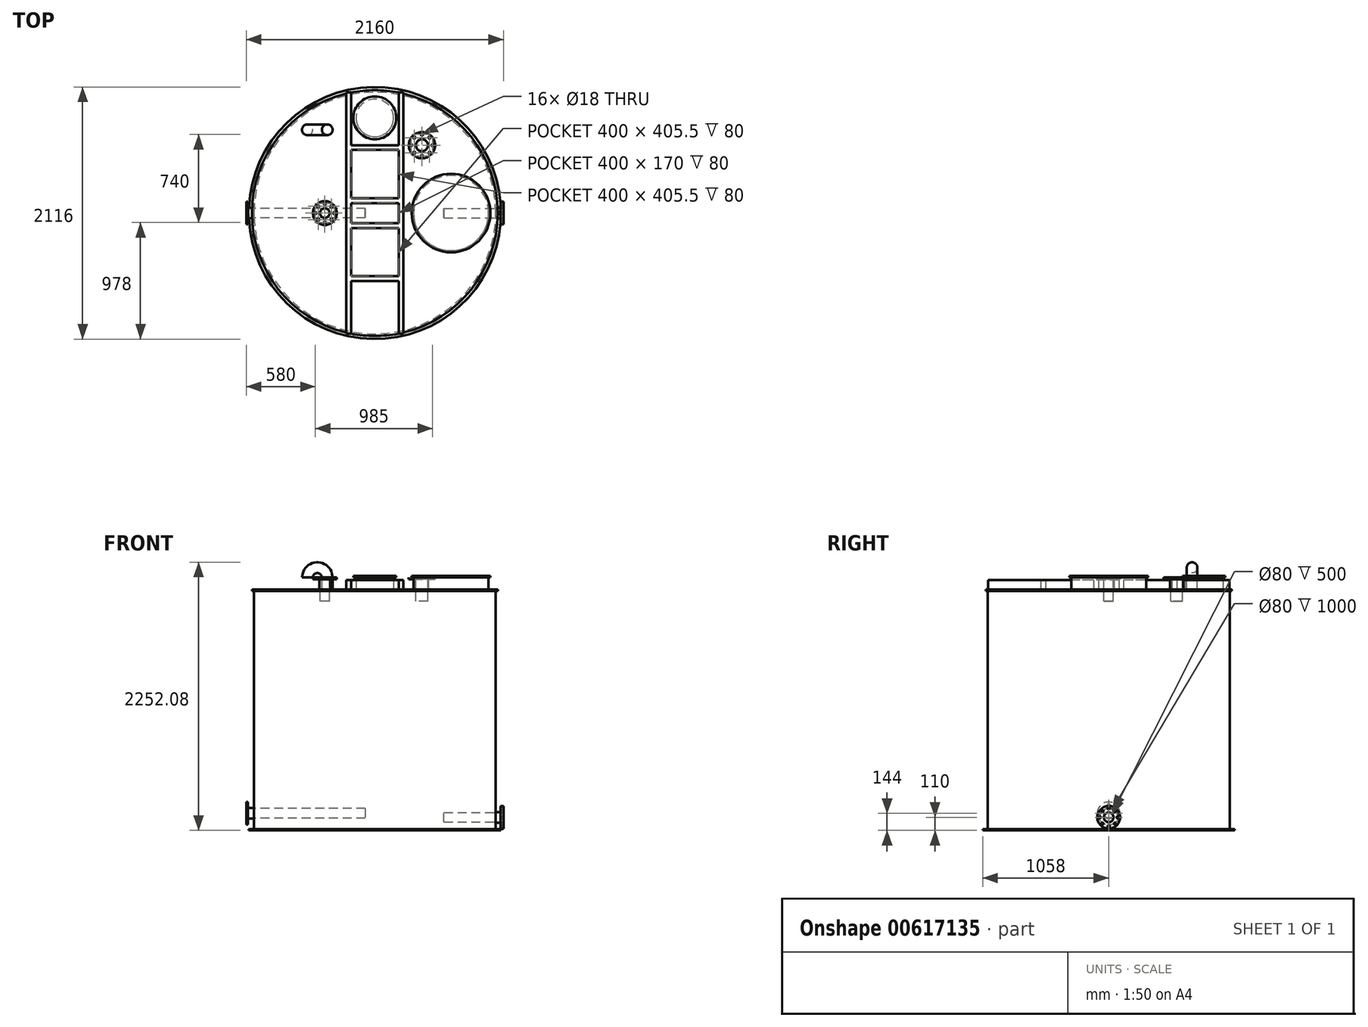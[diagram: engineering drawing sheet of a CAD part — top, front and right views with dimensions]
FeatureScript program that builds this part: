
annotation { "Feature Type Name" : "Feature", "Feature Type Description" : "" }
export const myFeature = defineFeature(function(context is Context, id is Id, definition is map)
    precondition{}
    {
        {
            var Q0;
            Q0=qCreatedBy(makeId("Front.planeOp"),FACE);
            var sketch = newSketch(context, id + "F0", { "sketchPlane" : qUnion([Q0])});
            skLineSegment(sketch, "E0.bottom", {"start": v(0, 0) * mm, "end": v(1015, 0) * mm});
            skLineSegment(sketch, "E0.top", {"start": v(0, 2024) * mm, "end": v(1015, 2024) * mm});
            skLineSegment(sketch, "E0.left", {"start": v(0, 0) * mm, "end": v(0, 2024) * mm});
            skLineSegment(sketch, "E0.right", {"start": v(1015, 12) * mm, "end": v(1015, 2012) * mm});
            skLineSegment(sketch, "E1.bottom", {"start": v(1015, 0) * mm, "end": v(1058, 0) * mm});
            skLineSegment(sketch, "E1.top", {"start": v(1015, 12) * mm, "end": v(1058, 12) * mm});
            skLineSegment(sketch, "E1.right", {"start": v(1058, 0) * mm, "end": v(1058, 12) * mm});
            skLineSegment(sketch, "E2.bottom", {"start": v(1015, 2024) * mm, "end": v(1032, 2024) * mm});
            skLineSegment(sketch, "E2.top", {"start": v(1015, 2012) * mm, "end": v(1032, 2012) * mm});
            skLineSegment(sketch, "E2.right", {"start": v(1032, 2024) * mm, "end": v(1032, 2012) * mm});
            skSolve(sketch);
        }
        {
            var Q0;
            Q0=makeQuery(id+"F0.imprint","IMPRINT",FACE,{"disambiguationData":[TD([[makeQuery(id+"F0.imprint","IMPRINT",EDGE,{"derivedFrom":sQuery(id+"F0.wireOp",EDGE,"E0.bottom")}),1.0]])]});
            var Q1;
            Q1=sQuery(id+"F0.wireOp",EDGE,"E0.left");
            revolve(context, id + "F1", {"entities" : qUnion([Q0]), "axis" : qUnion([Q1]), "revolveType" : RevolveType.FULL});
        }
        {
            var Q0;
            Q0=makeQuery(id+"F1.opRevolve","SWEPT_FACE",FACE,{"disambiguationData":[OSD([sQuery(id+"F0.wireOp",EDGE,"E0.top"),sQuery(id+"F0.wireOp",EDGE,"E2.bottom")])]});
            var sketch = newSketch(context, id + "F2", { "sketchPlane" : qUnion([Q0])});
            skLineSegment(sketch, "E3.bottom", {"start": v(-240, 1012.5) * mm, "end": v(-200, 1012.5) * mm});
            skLineSegment(sketch, "E3.top", {"start": v(-240, -1012.5) * mm, "end": v(-200, -1012.5) * mm});
            skLineSegment(sketch, "E3.left", {"start": v(-240, 1012.5) * mm, "end": v(-240, -1012.5) * mm});
            skLineSegment(sketch, "E3.right", {"start": v(-200, 1012.5) * mm, "end": v(-200, 570.5) * mm});
            skLineSegment(sketch, "E4.bottom", {"start": v(200, 1012.5) * mm, "end": v(240, 1012.5) * mm});
            skLineSegment(sketch, "E4.top", {"start": v(200, -1012.5) * mm, "end": v(240, -1012.5) * mm});
            skLineSegment(sketch, "E4.left", {"start": v(200, 1012.5) * mm, "end": v(200, 570.5) * mm});
            skLineSegment(sketch, "E4.right", {"start": v(240, 1012.5) * mm, "end": v(240, -1012.5) * mm});
            skLineSegment(sketch, "E5.bottom", {"start": v(-200, 85) * mm, "end": v(200, 85) * mm});
            skLineSegment(sketch, "E5.top", {"start": v(-200, 125) * mm, "end": v(200, 125) * mm});
            skLineSegment(sketch, "E6.bottom", {"start": v(-200, -85) * mm, "end": v(200, -85) * mm});
            skLineSegment(sketch, "E6.top", {"start": v(-200, -125) * mm, "end": v(200, -125) * mm});
            skLineSegment(sketch, "E7.bottom", {"start": v(-200, 570.5) * mm, "end": v(200, 570.5) * mm});
            skLineSegment(sketch, "E7.top", {"start": v(-200, 530.5) * mm, "end": v(200, 530.5) * mm});
            skLineSegment(sketch, "E8.bottom", {"start": v(-200, -530.5) * mm, "end": v(200, -530.5) * mm});
            skLineSegment(sketch, "E8.top", {"start": v(-200, -570.5) * mm, "end": v(200, -570.5) * mm});
            skLineSegment(sketch, "E9.trimOffspring", {"start": v(-200, 530.5) * mm, "end": v(-200, 125) * mm});
            skLineSegment(sketch, "E10.trimOffspring", {"start": v(200, 530.5) * mm, "end": v(200, 125) * mm});
            skLineSegment(sketch, "E11.trimOffspring", {"start": v(-200, 85) * mm, "end": v(-200, -85) * mm});
            skLineSegment(sketch, "E12.trimOffspring", {"start": v(200, 85) * mm, "end": v(200, -85) * mm});
            skLineSegment(sketch, "E13.trimOffspring", {"start": v(-200, -125) * mm, "end": v(-200, -530.5) * mm});
            skLineSegment(sketch, "E14.trimOffspring", {"start": v(200, -125) * mm, "end": v(200, -530.5) * mm});
            skLineSegment(sketch, "E15.trimOffspring", {"start": v(-200, -570.5) * mm, "end": v(-200, -1012.5) * mm});
            skLineSegment(sketch, "E16.trimOffspring", {"start": v(200, -570.5) * mm, "end": v(200, -1012.5) * mm});
            skSolve(sketch);
        }
        {
            var Q0;
            Q0 = qSketchRegion(id + "F2", true);
            extrude(context, id + "F3", {"entities" : qUnion([Q0]), "operationType" : NewBodyOperationType.ADD, "depth" : 80 * mm, "offsetDistance" : 25 * mm});
        }
        {
            var Q0;
            {var subQ0=sQuery(id+"F2.wireOp",EDGE,"E4.right");Q0=makeQuery(id+"F3.boolean.opBoolean","SPLIT",FACE,{"disambiguationData":[TD([makeQuery(id+"F3.opExtrude","SWEPT_FACE",FACE,{"disambiguationData":[OSD([subQ0])]})])],"derivedFrom":makeQuery(id+"F1.opRevolve","SWEPT_FACE",FACE,{"disambiguationData":[OSD([sQuery(id+"F0.wireOp",EDGE,"E0.top"),sQuery(id+"F0.wireOp",EDGE,"E2.bottom")])]})});}
            var sketch = newSketch(context, id + "F4", { "sketchPlane" : qUnion([Q0])});
            skCircle(sketch, "E17", {"center": v(640, 0) * mm, "radius": 315 * mm});
            skSolve(sketch);
        }
        {
            var Q0;
            Q0=makeQuery(id+"F4.imprint","IMPRINT",FACE,{"disambiguationData":[TD([[makeQuery(id+"F4.imprint","IMPRINT",EDGE,{"derivedFrom":sQuery(id+"F4.wireOp",EDGE,"E17")}),1.0]])]});
            extrude(context, id + "F5", {"entities" : qUnion([Q0]), "operationType" : NewBodyOperationType.ADD, "depth" : 100 * mm, "offsetDistance" : 25 * mm});
        }
        {
            var Q0;
            Q0=makeQuery(id+"F5.opExtrude","CAP_FACE",FACE,{"disambiguationData":[OSD([sQuery(id+"F4.wireOp",EDGE,"E17")])],"isStart":false});
            var sketch = newSketch(context, id + "F6", { "sketchPlane" : qUnion([Q0])});
            skCircle(sketch, "E18", {"center": v(640, 0) * mm, "radius": 330 * mm});
            skSolve(sketch);
        }
        {
            var Q0;
            Q0 = qSketchRegion(id + "F6", true);
            extrude(context, id + "F7", {"entities" : qUnion([Q0]), "operationType" : NewBodyOperationType.ADD, "depth" : 15 * mm, "offsetDistance" : 25 * mm});
        }
        {
            var Q0;
            {var subQ0=sQuery(id+"F2.wireOp",EDGE,"E3.left");Q0=makeQuery(id+"F3.boolean.opBoolean","SPLIT",FACE,{"disambiguationData":[TD([makeQuery(id+"F3.opExtrude","SWEPT_FACE",FACE,{"disambiguationData":[OSD([subQ0])]})])],"derivedFrom":makeQuery(id+"F1.opRevolve","SWEPT_FACE",FACE,{"disambiguationData":[OSD([sQuery(id+"F0.wireOp",EDGE,"E0.top"),sQuery(id+"F0.wireOp",EDGE,"E2.bottom")])]})});}
            var sketch = newSketch(context, id + "F8", { "sketchPlane" : qUnion([Q0])});
            skCircle(sketch, "E19", {"center": v(-420, 0) * mm, "radius": 45 * mm});
            skSolve(sketch);
        }
        {
            var Q0;
            Q0=makeQuery(id+"F8.imprint","IMPRINT",FACE,{"disambiguationData":[TD([[makeQuery(id+"F8.imprint","IMPRINT",EDGE,{"derivedFrom":sQuery(id+"F8.wireOp",EDGE,"E19")}),1.0]])]});
            extrude(context, id + "F9", {"entities" : qUnion([Q0]), "operationType" : NewBodyOperationType.ADD, "depth" : 100 * mm, "offsetDistance" : 25 * mm});
        }
        {
            var Q0;
            Q0=makeQuery(id+"F9.opExtrude","CAP_FACE",FACE,{"disambiguationData":[OSD([sQuery(id+"F8.wireOp",EDGE,"E19")])],"isStart":false});
            var sketch = newSketch(context, id + "F10", { "sketchPlane" : qUnion([Q0])});
            skCircle(sketch, "E20", {"center": v(-420, 0) * mm, "radius": 100 * mm});
            skCircle(sketch, "E21", {"center": v(-420, 80) * mm, "radius": 9 * mm});
            skCircle(sketch, "E22.1.0", {"center": v(-476.57, 56.57) * mm, "radius": 9 * mm});
            skCircle(sketch, "E22.2.0", {"center": v(-500, 0) * mm, "radius": 9 * mm});
            skCircle(sketch, "E22.3.0", {"center": v(-476.57, -56.57) * mm, "radius": 9 * mm});
            skCircle(sketch, "E22.4.0", {"center": v(-420, -80) * mm, "radius": 9 * mm});
            skCircle(sketch, "E22.5.0", {"center": v(-363.43, -56.57) * mm, "radius": 9 * mm});
            skCircle(sketch, "E22.6.0", {"center": v(-340, 0) * mm, "radius": 9 * mm});
            skCircle(sketch, "E22.7.0", {"center": v(-363.43, 56.57) * mm, "radius": 9 * mm});
            skSolve(sketch);
        }
        {
            var Q0;
            Q0 = qSketchRegion(id + "F10", true);
            extrude(context, id + "F11", {"entities" : qUnion([Q0]), "operationType" : NewBodyOperationType.ADD, "oppositeDirection" : true, "depth" : 15 * mm, "offsetDistance" : 25 * mm});
        }
        {
            var Q0;
            Q0=makeQuery(id+"F11.boolean.opBoolean","MERGE",FACE,{"derivedFrom":[makeQuery(id+"F9.opExtrude","CAP_FACE",FACE,{"disambiguationData":[OSD([sQuery(id+"F8.wireOp",EDGE,"E19")])],"isStart":false}),makeQuery(id+"F11.opExtrude","CAP_FACE",FACE,{"disambiguationData":[OSD([sQuery(id+"F10.wireOp",EDGE,"E20"),sQuery(id+"F10.wireOp",EDGE,"E21"),sQuery(id+"F10.wireOp",EDGE,"E22.1.0"),sQuery(id+"F10.wireOp",EDGE,"E22.2.0"),sQuery(id+"F10.wireOp",EDGE,"E22.3.0"),sQuery(id+"F10.wireOp",EDGE,"E22.4.0"),sQuery(id+"F10.wireOp",EDGE,"E22.5.0"),sQuery(id+"F10.wireOp",EDGE,"E22.6.0"),sQuery(id+"F10.wireOp",EDGE,"E22.7.0")])],"isStart":true})]});
            var sketch = newSketch(context, id + "F12", { "sketchPlane" : qUnion([Q0])});
            skCircle(sketch, "E23", {"center": v(-420, 0) * mm, "radius": 40 * mm});
            skSolve(sketch);
        }
        {
            var Q0;
            Q0=makeQuery(id+"F12.imprint","IMPRINT",FACE,{"disambiguationData":[TD([[makeQuery(id+"F12.imprint","IMPRINT",EDGE,{"derivedFrom":sQuery(id+"F12.wireOp",EDGE,"E23")}),1.0]])]});
            extrude(context, id + "F13", {"entities" : qUnion([Q0]), "operationType" : NewBodyOperationType.REMOVE, "oppositeDirection" : true, "depth" : 200 * mm, "offsetDistance" : 25 * mm});
        }
        {
            var Q0;
            {var subQ0=sQuery(id+"F2.wireOp",EDGE,"E3.right");Q0=makeQuery(id+"F3.boolean.opBoolean","SPLIT",FACE,{"disambiguationData":[TD([makeQuery(id+"F3.opExtrude","SWEPT_FACE",FACE,{"disambiguationData":[OSD([subQ0])]})])],"derivedFrom":makeQuery(id+"F1.opRevolve","SWEPT_FACE",FACE,{"disambiguationData":[OSD([sQuery(id+"F0.wireOp",EDGE,"E0.top"),sQuery(id+"F0.wireOp",EDGE,"E2.bottom")])]})});}
            var sketch = newSketch(context, id + "F14", { "sketchPlane" : qUnion([Q0])});
            skCircle(sketch, "E24", {"center": v(0, 800) * mm, "radius": 158 * mm});
            skSolve(sketch);
        }
        {
            var Q0;
            Q0=makeQuery(id+"F14.imprint","IMPRINT",FACE,{"disambiguationData":[TD([[makeQuery(id+"F14.imprint","IMPRINT",EDGE,{"derivedFrom":sQuery(id+"F14.wireOp",EDGE,"E24")}),1.0]])]});
            extrude(context, id + "F15", {"entities" : qUnion([Q0]), "operationType" : NewBodyOperationType.ADD, "depth" : 100 * mm, "offsetDistance" : 25 * mm});
        }
        {
            var Q0;
            Q0=makeQuery(id+"F15.opExtrude","CAP_FACE",FACE,{"disambiguationData":[OSD([sQuery(id+"F14.wireOp",EDGE,"E24")])],"isStart":false});
            var sketch = newSketch(context, id + "F16", { "sketchPlane" : qUnion([Q0])});
            skCircle(sketch, "E25", {"center": v(0, 800) * mm, "radius": 180 * mm});
            skSolve(sketch);
        }
        {
            var Q0;
            Q0 = qSketchRegion(id + "F16", true);
            extrude(context, id + "F17", {"entities" : qUnion([Q0]), "operationType" : NewBodyOperationType.ADD, "depth" : 15 * mm, "offsetDistance" : 25 * mm});
        }
        {
            var Q0;
            {var subQ0=sQuery(id+"F2.wireOp",EDGE,"E4.right");Q0=makeQuery(id+"F3.boolean.opBoolean","SPLIT",FACE,{"disambiguationData":[TD([makeQuery(id+"F3.opExtrude","SWEPT_FACE",FACE,{"disambiguationData":[OSD([subQ0])]})])],"derivedFrom":makeQuery(id+"F1.opRevolve","SWEPT_FACE",FACE,{"disambiguationData":[OSD([sQuery(id+"F0.wireOp",EDGE,"E0.top"),sQuery(id+"F0.wireOp",EDGE,"E2.bottom")])]})});}
            var sketch = newSketch(context, id + "F18", { "sketchPlane" : qUnion([Q0])});
            skCircle(sketch, "E26", {"center": v(395, 570) * mm, "radius": 55 * mm});
            skSolve(sketch);
        }
        {
            var Q0;
            Q0=makeQuery(id+"F18.imprint","IMPRINT",FACE,{"disambiguationData":[TD([[makeQuery(id+"F18.imprint","IMPRINT",EDGE,{"derivedFrom":sQuery(id+"F18.wireOp",EDGE,"E26")}),1.0]])]});
            var Q1;
            Q1=sQuery(id+"F18.wireOp",EDGE,"E26");
            extrude(context, id + "F19", {"entities" : qUnion([Q0]), "operationType" : NewBodyOperationType.ADD, "surfaceEntities" : qUnion([Q1]), "depth" : 100 * mm, "offsetDistance" : 25 * mm});
        }
        {
            var Q0;
            Q0=makeQuery(id+"F19.opExtrude","CAP_FACE",FACE,{"disambiguationData":[OSD([sQuery(id+"F18.wireOp",EDGE,"E26")])],"isStart":false});
            var sketch = newSketch(context, id + "F20", { "sketchPlane" : qUnion([Q0])});
            skCircle(sketch, "E27", {"center": v(395, 570) * mm, "radius": 110 * mm});
            skCircle(sketch, "E28", {"center": v(395, 480) * mm, "radius": 9 * mm});
            skCircle(sketch, "E29.1.0", {"center": v(458.64, 506.36) * mm, "radius": 9 * mm});
            skCircle(sketch, "E29.2.0", {"center": v(485, 570) * mm, "radius": 9 * mm});
            skCircle(sketch, "E29.3.0", {"center": v(458.64, 633.64) * mm, "radius": 9 * mm});
            skCircle(sketch, "E29.4.0", {"center": v(395, 660) * mm, "radius": 9 * mm});
            skCircle(sketch, "E29.5.0", {"center": v(331.36, 633.64) * mm, "radius": 9 * mm});
            skCircle(sketch, "E29.6.0", {"center": v(305, 570) * mm, "radius": 9 * mm});
            skCircle(sketch, "E29.7.0", {"center": v(331.36, 506.36) * mm, "radius": 9 * mm});
            skSolve(sketch);
        }
        {
            var Q0;
            Q0=makeQuery(id+"F20.imprint","IMPRINT",FACE,{"disambiguationData":[TD([[makeQuery(id+"F20.imprint","IMPRINT",EDGE,{"derivedFrom":sQuery(id+"F20.wireOp",EDGE,"E27")}),1.0]])]});
            extrude(context, id + "F21", {"entities" : qUnion([Q0]), "operationType" : NewBodyOperationType.ADD, "oppositeDirection" : true, "depth" : 15 * mm, "offsetDistance" : 25 * mm});
        }
        {
            var Q0;
            {var subQ0=sQuery(id+"F18.wireOp",EDGE,"E26");Q0=makeQuery(id+"F21.boolean.opBoolean","MERGE",FACE,{"derivedFrom":[makeQuery(id+"F19.opExtrude","CAP_FACE",FACE,{"disambiguationData":[OSD([subQ0])],"isStart":false}),makeQuery(id+"F21.opExtrude","CAP_FACE",FACE,{"disambiguationData":[OSD([subQ0,sQuery(id+"F20.wireOp",EDGE,"E27"),sQuery(id+"F20.wireOp",EDGE,"E28"),sQuery(id+"F20.wireOp",EDGE,"E29.1.0"),sQuery(id+"F20.wireOp",EDGE,"E29.2.0"),sQuery(id+"F20.wireOp",EDGE,"E29.3.0"),sQuery(id+"F20.wireOp",EDGE,"E29.4.0"),sQuery(id+"F20.wireOp",EDGE,"E29.5.0"),sQuery(id+"F20.wireOp",EDGE,"E29.6.0"),sQuery(id+"F20.wireOp",EDGE,"E29.7.0")])],"isStart":true})]});}
            var sketch = newSketch(context, id + "F22", { "sketchPlane" : qUnion([Q0])});
            skCircle(sketch, "E30", {"center": v(395, 570) * mm, "radius": 50 * mm});
            skSolve(sketch);
        }
        {
            var Q0;
            Q0=makeQuery(id+"F22.imprint","IMPRINT",FACE,{"disambiguationData":[TD([[makeQuery(id+"F22.imprint","IMPRINT",EDGE,{"derivedFrom":sQuery(id+"F22.wireOp",EDGE,"E30")}),1.0]])]});
            extrude(context, id + "F23", {"entities" : qUnion([Q0]), "operationType" : NewBodyOperationType.REMOVE, "oppositeDirection" : true, "depth" : 200 * mm, "offsetDistance" : 25 * mm});
        }
        {
            var Q0;
            {var subQ0=sQuery(id+"F2.wireOp",EDGE,"E3.left");Q0=makeQuery(id+"F3.boolean.opBoolean","SPLIT",FACE,{"disambiguationData":[TD([makeQuery(id+"F3.opExtrude","SWEPT_FACE",FACE,{"disambiguationData":[OSD([subQ0])]})])],"derivedFrom":makeQuery(id+"F1.opRevolve","SWEPT_FACE",FACE,{"disambiguationData":[OSD([sQuery(id+"F0.wireOp",EDGE,"E0.top"),sQuery(id+"F0.wireOp",EDGE,"E2.bottom")])]})});}
            var sketch = newSketch(context, id + "F24", { "sketchPlane" : qUnion([Q0])});
            skCircle(sketch, "E31", {"center": v(-400, 700) * mm, "radius": 45 * mm});
            skSolve(sketch);
        }
        {
            var Q0;
            Q0=qCreatedBy(makeId("Front.planeOp"),FACE);
            cPlane(context, id + "F25", {"entities" : qUnion([Q0]), "cplaneType" : CPlaneType.OFFSET, "offset" : 700 * mm, "oppositeDirection" : true, "width" : 150 * mm, "height" : 150 * mm});
        }
        {
            var Q0;
            Q0=qCreatedBy(id+"F25.planeOp",FACE);
            var sketch = newSketch(context, id + "F26", { "sketchPlane" : qUnion([Q0])});
            skPoint(sketch, "E32.0", {"position": v(-400, 2024) * mm});
            skLineSegment(sketch, "E33", {"start": v(-400, 2024) * mm, "end": v(-400, 2124) * mm});
            skPoint(sketch, "E34.third.point", {"position": v(-442.55, 2173.22) * mm});
            skArc(sketch, "E35", {"start": v(-400, 2124) * mm, "mid": v(-483.08, 2207.08) * mm, "end": v(-566.16, 2124) * mm});
            skSolve(sketch);
        }
        {
            var Q0;
            Q0=makeQuery(id+"F24.imprint","IMPRINT",FACE,{"disambiguationData":[TD([[makeQuery(id+"F24.imprint","IMPRINT",EDGE,{"derivedFrom":sQuery(id+"F24.wireOp",EDGE,"E31")}),1.0]])]});
            var Q1;
            Q1=sQuery(id+"F26.wireOp",EDGE,"E33");
            var Q2;
            Q2=sQuery(id+"F26.wireOp",EDGE,"E35");
            sweep(context, id + "F27", {"operationType" : NewBodyOperationType.ADD, "profiles" : qUnion([Q0]), "path" : qUnion([Q1, Q2])});
        }
        {
            var Q0;
            Q0=qCreatedBy(makeId("Right.planeOp"),FACE);
            var sketch = newSketch(context, id + "F28", { "sketchPlane" : qUnion([Q0])});
            skCircle(sketch, "E36", {"center": v(0, 110) * mm, "radius": 45 * mm});
            skSolve(sketch);
        }
        {
            var Q0;
            Q0 = qSketchRegion(id + "F28", true);
            var Q1;
            Q1=sQuery(id+"F28.wireOp",EDGE,"E36");
            extrude(context, id + "F29", {"entities" : qUnion([Q0]), "operationType" : NewBodyOperationType.ADD, "surfaceEntities" : qUnion([Q1]), "depth" : 1080 * mm, "offsetDistance" : 25 * mm});
        }
        {
            var Q0;
            Q0=makeQuery(id+"F29.opExtrude","CAP_FACE",FACE,{"disambiguationData":[OSD([sQuery(id+"F28.wireOp",EDGE,"E36")])],"isStart":false});
            var sketch = newSketch(context, id + "F30", { "sketchPlane" : qUnion([Q0])});
            skCircle(sketch, "E37", {"center": v(0, 110) * mm, "radius": 95 * mm});
            skCircle(sketch, "E38", {"center": v(0, 185) * mm, "radius": 9 * mm});
            skCircle(sketch, "E39.1.0", {"center": v(-53.03, 163.03) * mm, "radius": 9 * mm});
            skCircle(sketch, "E39.2.0", {"center": v(-75, 110) * mm, "radius": 9 * mm});
            skCircle(sketch, "E39.3.0", {"center": v(-53.03, 56.97) * mm, "radius": 9 * mm});
            skCircle(sketch, "E39.4.0", {"center": v(0, 35) * mm, "radius": 9 * mm});
            skCircle(sketch, "E39.5.0", {"center": v(53.03, 56.97) * mm, "radius": 9 * mm});
            skCircle(sketch, "E39.6.0", {"center": v(75, 110) * mm, "radius": 9 * mm});
            skCircle(sketch, "E39.7.0", {"center": v(53.03, 163.03) * mm, "radius": 9 * mm});
            skSolve(sketch);
        }
        {
            var Q0;
            Q0 = qSketchRegion(id + "F30", true);
            extrude(context, id + "F31", {"entities" : qUnion([Q0]), "operationType" : NewBodyOperationType.ADD, "oppositeDirection" : true, "depth" : 25 * mm, "offsetDistance" : 25 * mm});
        }
        {
            var Q0;
            Q0=makeQuery(id+"F31.boolean.opBoolean","MERGE",FACE,{"derivedFrom":[makeQuery(id+"F29.opExtrude","CAP_FACE",FACE,{"disambiguationData":[OSD([sQuery(id+"F28.wireOp",EDGE,"E36")])],"isStart":false}),makeQuery(id+"F31.opExtrude","CAP_FACE",FACE,{"disambiguationData":[OSD([sQuery(id+"F30.wireOp",EDGE,"E37"),sQuery(id+"F30.wireOp",EDGE,"E38"),sQuery(id+"F30.wireOp",EDGE,"E39.1.0"),sQuery(id+"F30.wireOp",EDGE,"E39.2.0"),sQuery(id+"F30.wireOp",EDGE,"E39.3.0"),sQuery(id+"F30.wireOp",EDGE,"E39.4.0"),sQuery(id+"F30.wireOp",EDGE,"E39.5.0"),sQuery(id+"F30.wireOp",EDGE,"E39.6.0"),sQuery(id+"F30.wireOp",EDGE,"E39.7.0")])],"isStart":true})]});
            var sketch = newSketch(context, id + "F32", { "sketchPlane" : qUnion([Q0])});
            skCircle(sketch, "E40", {"center": v(0, 110) * mm, "radius": 40 * mm});
            skSolve(sketch);
        }
        {
            var Q0;
            Q0=makeQuery(id+"F32.imprint","IMPRINT",FACE,{"disambiguationData":[TD([[makeQuery(id+"F32.imprint","IMPRINT",EDGE,{"derivedFrom":sQuery(id+"F32.wireOp",EDGE,"E40")}),1.0]])]});
            extrude(context, id + "F33", {"entities" : qUnion([Q0]), "operationType" : NewBodyOperationType.REMOVE, "oppositeDirection" : true, "depth" : 500 * mm, "offsetDistance" : 25 * mm});
        }
        {
            var Q0;
            Q0=qCreatedBy(makeId("Right.planeOp"),FACE);
            var sketch = newSketch(context, id + "F34", { "sketchPlane" : qUnion([Q0])});
            skCircle(sketch, "E41", {"center": v(0, 144) * mm, "radius": 45 * mm});
            skSolve(sketch);
        }
        {
            var Q0;
            Q0 = qSketchRegion(id + "F34", true);
            extrude(context, id + "F35", {"entities" : qUnion([Q0]), "operationType" : NewBodyOperationType.ADD, "oppositeDirection" : true, "depth" : 1080 * mm, "offsetDistance" : 25 * mm});
        }
        {
            var Q0;
            Q0=makeQuery(id+"F35.opExtrude","CAP_FACE",FACE,{"disambiguationData":[OSD([sQuery(id+"F34.wireOp",EDGE,"E41")])],"isStart":false});
            var sketch = newSketch(context, id + "F36", { "sketchPlane" : qUnion([Q0])});
            skCircle(sketch, "E42", {"center": v(0, 144) * mm, "radius": 95 * mm});
            skCircle(sketch, "E43", {"center": v(0, 219) * mm, "radius": 9 * mm});
            skCircle(sketch, "E44.1.0", {"center": v(-75, 144) * mm, "radius": 9 * mm});
            skCircle(sketch, "E44.2.0", {"center": v(0, 69) * mm, "radius": 9 * mm});
            skCircle(sketch, "E44.3.0", {"center": v(75, 144) * mm, "radius": 9 * mm});
            skSolve(sketch);
        }
        {
            var Q0;
            Q0 = qSketchRegion(id + "F36", true);
            extrude(context, id + "F37", {"entities" : qUnion([Q0]), "operationType" : NewBodyOperationType.ADD, "oppositeDirection" : true, "depth" : 15 * mm, "offsetDistance" : 25 * mm});
        }
        {
            var Q0;
            Q0=makeQuery(id+"F37.boolean.opBoolean","MERGE",FACE,{"derivedFrom":[makeQuery(id+"F35.opExtrude","CAP_FACE",FACE,{"disambiguationData":[OSD([sQuery(id+"F34.wireOp",EDGE,"E41")])],"isStart":false}),makeQuery(id+"F37.opExtrude","CAP_FACE",FACE,{"disambiguationData":[OSD([sQuery(id+"F36.wireOp",EDGE,"E42"),sQuery(id+"F36.wireOp",EDGE,"E43"),sQuery(id+"F36.wireOp",EDGE,"E44.1.0"),sQuery(id+"F36.wireOp",EDGE,"E44.2.0"),sQuery(id+"F36.wireOp",EDGE,"E44.3.0")])],"isStart":true})]});
            var sketch = newSketch(context, id + "F38", { "sketchPlane" : qUnion([Q0])});
            skCircle(sketch, "E45", {"center": v(0, 144) * mm, "radius": 40 * mm});
            skSolve(sketch);
        }
        {
            var Q0;
            Q0=makeQuery(id+"F38.imprint","IMPRINT",FACE,{"disambiguationData":[TD([[makeQuery(id+"F38.imprint","IMPRINT",EDGE,{"derivedFrom":sQuery(id+"F38.wireOp",EDGE,"E45")}),1.0]])]});
            extrude(context, id + "F39", {"entities" : qUnion([Q0]), "operationType" : NewBodyOperationType.REMOVE, "oppositeDirection" : true, "depth" : 1000 * mm, "offsetDistance" : 25 * mm});
        }
    });
